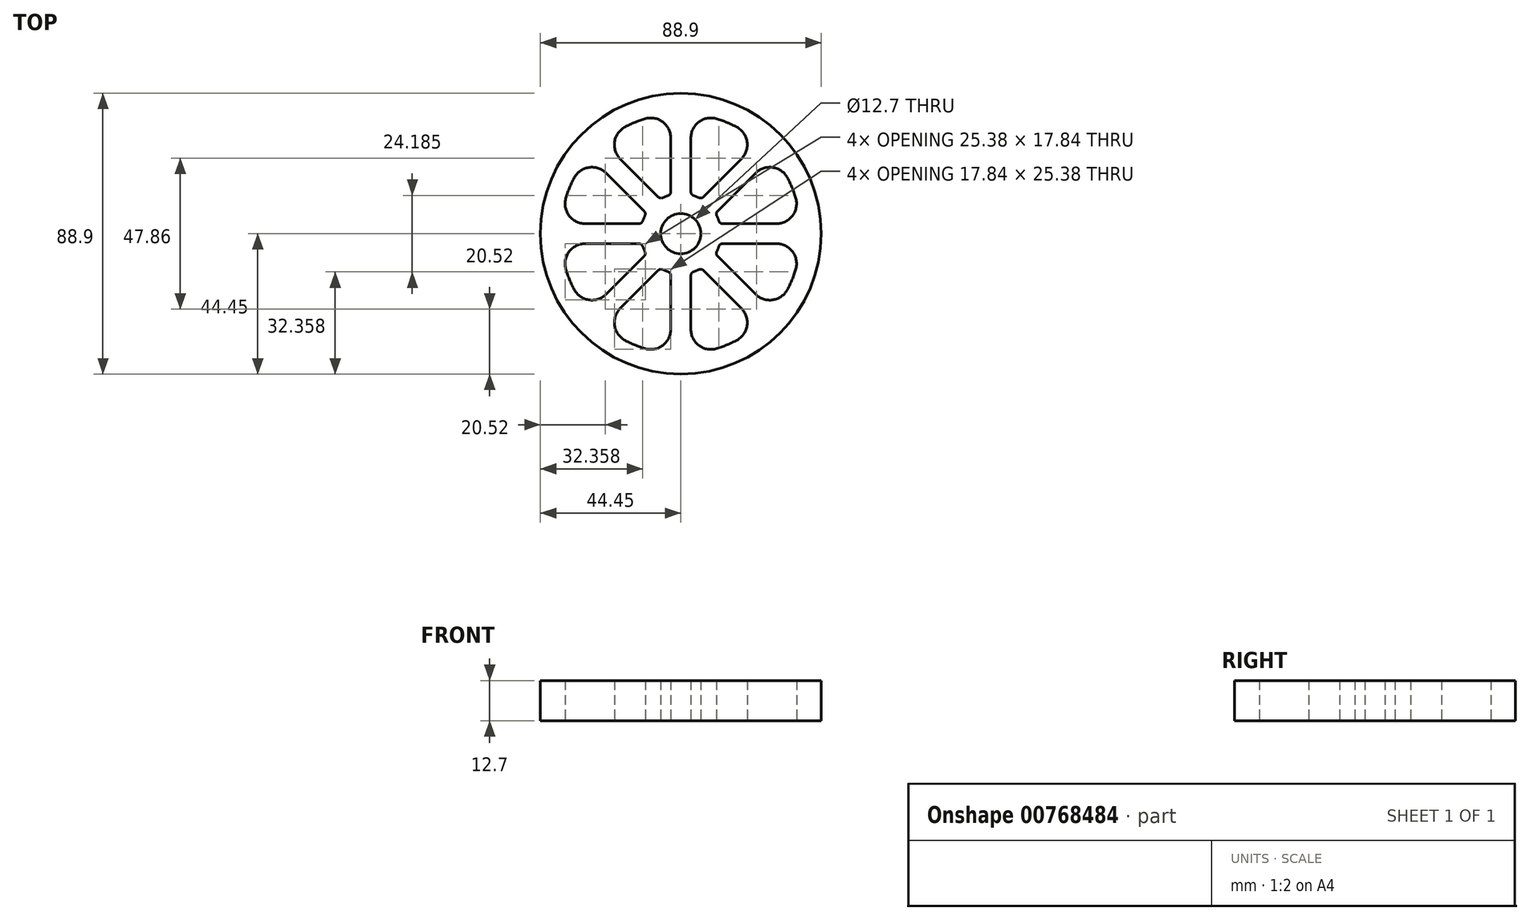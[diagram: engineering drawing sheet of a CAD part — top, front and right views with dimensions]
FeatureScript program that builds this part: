
annotation { "Feature Type Name" : "Feature", "Feature Type Description" : "" }
export const myFeature = defineFeature(function(context is Context, id is Id, definition is map)
    precondition{}
    {
        {
            var Q0;
            Q0=qCreatedBy(makeId("Top.planeOp"),FACE);
            var sketch = newSketch(context, id + "F0", { "sketchPlane" : qUnion([Q0])});
            skCircle(sketch, "E0", {"center": v(0, 0) * mm, "radius": 44.45 * mm});
            skArc(sketch, "E1", {"start": v(-11.43, 36.35) * mm, "mid": v(-14.58, 35.2) * mm, "end": v(-17.62, 33.78) * mm});
            skArc(sketch, "E2", {"start": v(12.04, 4.04) * mm, "mid": v(11.73, 4.86) * mm, "end": v(11.37, 5.66) * mm});
            skCircle(sketch, "E3", {"center": v(0, 0) * mm, "radius": 6.35 * mm});
            skLineSegment(sketch, "E4", {"start": v(-3.18, 30.29) * mm, "end": v(-3.17, 13.24) * mm});
            skLineSegment(sketch, "E5", {"start": v(3.18, 30.29) * mm, "end": v(3.18, 13.24) * mm});
            skLineSegment(sketch, "E6", {"start": v(13.24, 3.17) * mm, "end": v(30.29, 3.18) * mm});
            skLineSegment(sketch, "E7", {"start": v(13.24, -3.18) * mm, "end": v(30.29, -3.17) * mm});
            skLineSegment(sketch, "E8", {"start": v(3.18, -13.24) * mm, "end": v(3.18, -30.29) * mm});
            skLineSegment(sketch, "E9", {"start": v(-3.18, -13.24) * mm, "end": v(-3.18, -30.29) * mm});
            skLineSegment(sketch, "E10", {"start": v(-13.24, 3.18) * mm, "end": v(-30.29, 3.18) * mm});
            skLineSegment(sketch, "E11", {"start": v(-13.24, -3.18) * mm, "end": v(-30.29, -3.18) * mm});
            skArc(sketch, "E12.trimOffspring", {"start": v(-36.35, -11.43) * mm, "mid": v(-35.2, -14.58) * mm, "end": v(-33.78, -17.62) * mm});
            skArc(sketch, "E13.trimOffspring", {"start": v(11.43, -36.35) * mm, "mid": v(14.58, -35.2) * mm, "end": v(17.62, -33.78) * mm});
            skArc(sketch, "E14.trimOffspring", {"start": v(36.35, 11.43) * mm, "mid": v(35.2, 14.58) * mm, "end": v(33.78, 17.62) * mm});
            skArc(sketch, "E15.trimOffspring", {"start": v(-4.04, 12.04) * mm, "mid": v(-4.86, 11.73) * mm, "end": v(-5.66, 11.37) * mm});
            skArc(sketch, "E16.trimOffspring", {"start": v(-12.04, -4.04) * mm, "mid": v(-11.73, -4.86) * mm, "end": v(-11.37, -5.66) * mm});
            skArc(sketch, "E17.trimOffspring", {"start": v(4.04, -12.04) * mm, "mid": v(4.86, -11.73) * mm, "end": v(5.66, -11.37) * mm});
            skLineSegment(sketch, "E18", {"start": v(-31.43, 31.43) * mm, "end": v(31.43, -31.43) * mm, "construction": true});
            skLineSegment(sketch, "E19", {"start": v(-31.43, -31.43) * mm, "end": v(31.43, 31.43) * mm, "construction": true});
            skLineSegment(sketch, "E20", {"start": v(-19.17, 23.66) * mm, "end": v(-7.12, 11.6) * mm});
            skLineSegment(sketch, "E21.MirrorCS", {"start": v(-23.66, 19.17) * mm, "end": v(-11.6, 7.12) * mm});
            skLineSegment(sketch, "E22.MirrorCS", {"start": v(19.17, 23.66) * mm, "end": v(7.12, 11.6) * mm});
            skLineSegment(sketch, "E23.MirrorCS", {"start": v(23.66, 19.17) * mm, "end": v(11.6, 7.12) * mm});
            skLineSegment(sketch, "E24.MirrorCS", {"start": v(-19.17, -23.66) * mm, "end": v(-7.12, -11.6) * mm});
            skLineSegment(sketch, "E25.MirrorCS", {"start": v(-23.66, -19.17) * mm, "end": v(-11.6, -7.12) * mm});
            skLineSegment(sketch, "E26.MirrorCS", {"start": v(19.17, -23.66) * mm, "end": v(7.12, -11.6) * mm});
            skLineSegment(sketch, "E27.MirrorCS", {"start": v(23.66, -19.17) * mm, "end": v(11.6, -7.12) * mm});
            skArc(sketch, "E28.trimOffspring", {"start": v(-33.78, 17.62) * mm, "mid": v(-35.2, 14.58) * mm, "end": v(-36.35, 11.43) * mm});
            skArc(sketch, "E29.trimOffspring", {"start": v(17.62, 33.78) * mm, "mid": v(14.58, 35.2) * mm, "end": v(11.43, 36.35) * mm});
            skArc(sketch, "E30.trimOffspring", {"start": v(33.78, -17.62) * mm, "mid": v(35.2, -14.58) * mm, "end": v(36.35, -11.43) * mm});
            skArc(sketch, "E31.trimOffspring", {"start": v(-17.62, -33.78) * mm, "mid": v(-14.58, -35.2) * mm, "end": v(-11.43, -36.35) * mm});
            skArc(sketch, "E32.trimOffspring", {"start": v(-11.37, 5.66) * mm, "mid": v(-11.73, 4.86) * mm, "end": v(-12.04, 4.04) * mm});
            skArc(sketch, "E33.trimOffspring", {"start": v(5.66, 11.37) * mm, "mid": v(4.86, 11.73) * mm, "end": v(4.04, 12.04) * mm});
            skArc(sketch, "E34.trimOffspring", {"start": v(11.37, -5.66) * mm, "mid": v(11.73, -4.86) * mm, "end": v(12.04, -4.04) * mm});
            skArc(sketch, "E35.trimOffspring", {"start": v(-5.66, -11.37) * mm, "mid": v(-4.86, -11.73) * mm, "end": v(-4.04, -12.04) * mm});
            skPoint(sketch, "E36.visualSharp", {"position": v(29.1, 24.6) * mm});
            skArc(sketch, "E36.filletArc", {"start": v(33.78, 17.62) * mm, "mid": v(29.12, 20.96) * mm, "end": v(23.66, 19.17) * mm});
            skPoint(sketch, "E37.visualSharp", {"position": v(3.18, 37.97) * mm});
            skArc(sketch, "E37.filletArc", {"start": v(11.43, 36.35) * mm, "mid": v(5.77, 35.4) * mm, "end": v(3.17, 30.29) * mm});
            skPoint(sketch, "E38.visualSharp", {"position": v(-3.17, 37.97) * mm});
            skArc(sketch, "E38.filletArc", {"start": v(-3.18, 30.29) * mm, "mid": v(-5.77, 35.4) * mm, "end": v(-11.43, 36.35) * mm});
            skPoint(sketch, "E39.visualSharp", {"position": v(24.6, 29.1) * mm});
            skArc(sketch, "E39.filletArc", {"start": v(19.17, 23.66) * mm, "mid": v(20.96, 29.12) * mm, "end": v(17.62, 33.78) * mm});
            skPoint(sketch, "E40.visualSharp", {"position": v(-24.6, 29.1) * mm});
            skArc(sketch, "E40.filletArc", {"start": v(-17.62, 33.78) * mm, "mid": v(-20.96, 29.12) * mm, "end": v(-19.17, 23.66) * mm});
            skPoint(sketch, "E41.visualSharp", {"position": v(-29.1, 24.6) * mm});
            skArc(sketch, "E41.filletArc", {"start": v(-23.66, 19.17) * mm, "mid": v(-29.12, 20.96) * mm, "end": v(-33.78, 17.62) * mm});
            skPoint(sketch, "E42.visualSharp", {"position": v(-37.97, 3.18) * mm});
            skArc(sketch, "E42.filletArc", {"start": v(-36.35, 11.43) * mm, "mid": v(-35.4, 5.77) * mm, "end": v(-30.29, 3.17) * mm});
            skPoint(sketch, "E43.visualSharp", {"position": v(-37.97, -3.18) * mm});
            skArc(sketch, "E43.filletArc", {"start": v(-30.29, -3.18) * mm, "mid": v(-35.4, -5.77) * mm, "end": v(-36.35, -11.43) * mm});
            skPoint(sketch, "E44.visualSharp", {"position": v(-29.1, -24.6) * mm});
            skArc(sketch, "E44.filletArc", {"start": v(-33.78, -17.62) * mm, "mid": v(-29.12, -20.96) * mm, "end": v(-23.66, -19.17) * mm});
            skPoint(sketch, "E45.visualSharp", {"position": v(-24.6, -29.1) * mm});
            skArc(sketch, "E45.filletArc", {"start": v(-19.17, -23.66) * mm, "mid": v(-20.96, -29.12) * mm, "end": v(-17.62, -33.78) * mm});
            skPoint(sketch, "E46.visualSharp", {"position": v(-3.17, -37.97) * mm});
            skArc(sketch, "E46.filletArc", {"start": v(-11.43, -36.35) * mm, "mid": v(-5.77, -35.4) * mm, "end": v(-3.17, -30.29) * mm});
            skPoint(sketch, "E47.visualSharp", {"position": v(3.18, -37.97) * mm});
            skArc(sketch, "E47.filletArc", {"start": v(3.17, -30.29) * mm, "mid": v(5.77, -35.4) * mm, "end": v(11.43, -36.35) * mm});
            skPoint(sketch, "E48.visualSharp", {"position": v(24.6, -29.1) * mm});
            skArc(sketch, "E48.filletArc", {"start": v(17.62, -33.78) * mm, "mid": v(20.96, -29.12) * mm, "end": v(19.17, -23.66) * mm});
            skPoint(sketch, "E49.visualSharp", {"position": v(29.1, -24.6) * mm});
            skArc(sketch, "E49.filletArc", {"start": v(23.66, -19.17) * mm, "mid": v(29.12, -20.96) * mm, "end": v(33.78, -17.62) * mm});
            skPoint(sketch, "E50.visualSharp", {"position": v(37.97, -3.17) * mm});
            skArc(sketch, "E50.filletArc", {"start": v(36.35, -11.43) * mm, "mid": v(35.4, -5.77) * mm, "end": v(30.29, -3.18) * mm});
            skPoint(sketch, "E51.visualSharp", {"position": v(37.97, 3.18) * mm});
            skArc(sketch, "E51.filletArc", {"start": v(30.29, 3.18) * mm, "mid": v(35.4, 5.77) * mm, "end": v(36.35, 11.43) * mm});
            skPoint(sketch, "E52.visualSharp", {"position": v(10.94, 6.45) * mm});
            skArc(sketch, "E52.filletArc", {"start": v(11.6, 7.12) * mm, "mid": v(11.25, 6.43) * mm, "end": v(11.37, 5.66) * mm});
            skPoint(sketch, "E53.visualSharp", {"position": v(12.3, 3.17) * mm});
            skArc(sketch, "E53.filletArc", {"start": v(12.04, 4.04) * mm, "mid": v(12.5, 3.41) * mm, "end": v(13.24, 3.17) * mm});
            skPoint(sketch, "E54.visualSharp", {"position": v(6.45, 10.94) * mm});
            skArc(sketch, "E54.filletArc", {"start": v(5.66, 11.37) * mm, "mid": v(6.43, 11.25) * mm, "end": v(7.12, 11.6) * mm});
            skPoint(sketch, "E55.visualSharp", {"position": v(3.18, 12.3) * mm});
            skArc(sketch, "E55.filletArc", {"start": v(3.17, 13.24) * mm, "mid": v(3.41, 12.5) * mm, "end": v(4.04, 12.04) * mm});
            skPoint(sketch, "E56.visualSharp", {"position": v(-3.17, 12.3) * mm});
            skArc(sketch, "E56.filletArc", {"start": v(-4.04, 12.04) * mm, "mid": v(-3.41, 12.5) * mm, "end": v(-3.17, 13.24) * mm});
            skPoint(sketch, "E57.visualSharp", {"position": v(-6.45, 10.94) * mm});
            skArc(sketch, "E57.filletArc", {"start": v(-7.12, 11.6) * mm, "mid": v(-6.43, 11.25) * mm, "end": v(-5.66, 11.37) * mm});
            skPoint(sketch, "E58.visualSharp", {"position": v(-10.94, 6.45) * mm});
            skArc(sketch, "E58.filletArc", {"start": v(-11.37, 5.66) * mm, "mid": v(-11.25, 6.43) * mm, "end": v(-11.6, 7.12) * mm});
            skPoint(sketch, "E59.visualSharp", {"position": v(-12.3, 3.18) * mm});
            skArc(sketch, "E59.filletArc", {"start": v(-13.24, 3.18) * mm, "mid": v(-12.5, 3.41) * mm, "end": v(-12.04, 4.04) * mm});
            skPoint(sketch, "E60.visualSharp", {"position": v(-12.3, -3.17) * mm});
            skArc(sketch, "E60.filletArc", {"start": v(-12.04, -4.04) * mm, "mid": v(-12.5, -3.41) * mm, "end": v(-13.24, -3.17) * mm});
            skPoint(sketch, "E61.visualSharp", {"position": v(-10.94, -6.45) * mm});
            skArc(sketch, "E61.filletArc", {"start": v(-11.6, -7.12) * mm, "mid": v(-11.25, -6.43) * mm, "end": v(-11.37, -5.66) * mm});
            skPoint(sketch, "E62.visualSharp", {"position": v(-6.45, -10.94) * mm});
            skArc(sketch, "E62.filletArc", {"start": v(-5.66, -11.37) * mm, "mid": v(-6.43, -11.25) * mm, "end": v(-7.12, -11.6) * mm});
            skPoint(sketch, "E63.visualSharp", {"position": v(-3.17, -12.3) * mm});
            skArc(sketch, "E63.filletArc", {"start": v(-3.17, -13.24) * mm, "mid": v(-3.41, -12.5) * mm, "end": v(-4.04, -12.04) * mm});
            skPoint(sketch, "E64.visualSharp", {"position": v(3.18, -12.3) * mm});
            skArc(sketch, "E64.filletArc", {"start": v(4.04, -12.04) * mm, "mid": v(3.41, -12.5) * mm, "end": v(3.17, -13.24) * mm});
            skPoint(sketch, "E65.visualSharp", {"position": v(6.45, -10.94) * mm});
            skArc(sketch, "E65.filletArc", {"start": v(7.12, -11.6) * mm, "mid": v(6.43, -11.25) * mm, "end": v(5.66, -11.37) * mm});
            skPoint(sketch, "E66.visualSharp", {"position": v(10.94, -6.45) * mm});
            skArc(sketch, "E66.filletArc", {"start": v(11.37, -5.66) * mm, "mid": v(11.25, -6.43) * mm, "end": v(11.6, -7.12) * mm});
            skPoint(sketch, "E67.visualSharp", {"position": v(12.3, -3.18) * mm});
            skArc(sketch, "E67.filletArc", {"start": v(13.24, -3.18) * mm, "mid": v(12.5, -3.41) * mm, "end": v(12.04, -4.04) * mm});
            skSolve(sketch);
        }
        {
            var Q0;
            Q0=makeQuery(id+"F0.imprint","IMPRINT",FACE,{"disambiguationData":[TD([[makeQuery(id+"F0.imprint","IMPRINT",EDGE,{"derivedFrom":sQuery(id+"F0.wireOp",EDGE,"E0")}),1.0]])]});
            extrude(context, id + "F1", {"entities" : qUnion([Q0]), "depth" : 12.7 * mm, "offsetDistance" : 25.4 * mm});
        }
    });
